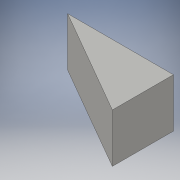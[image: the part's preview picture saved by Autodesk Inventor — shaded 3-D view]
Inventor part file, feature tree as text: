
AUTODESK INVENTOR PART (.ipt)
format: ipt  version: 2016 (Build 200138000, 138)  size: 88,064 bytes
history: native  units: in
note: dims shown in document units (in); Inventor stores cm internally (conversion verified against a paired STEP export)
features: extrude x1, sketch x1
ambient origin geometry x8: Origin, YZ Plane, XZ Plane, XY Plane, X Axis, Y Axis, Z Axis, Center Point
bodies: Body1 (feature_tree)
feature tree (2):
  extrude  "Extrusion2"  TaperAngle=150.0deg  [1 undecoded]
  sketch  "Sketch2"  dims[d4=19.685in d5=150.0deg d6=7.874in d7=0.0in]
note: 1 required parameter value undecoded (feature->parameter linkage not recoverable at this tier; creation-order binding heuristic only, values carry confidence <= 0.55)
